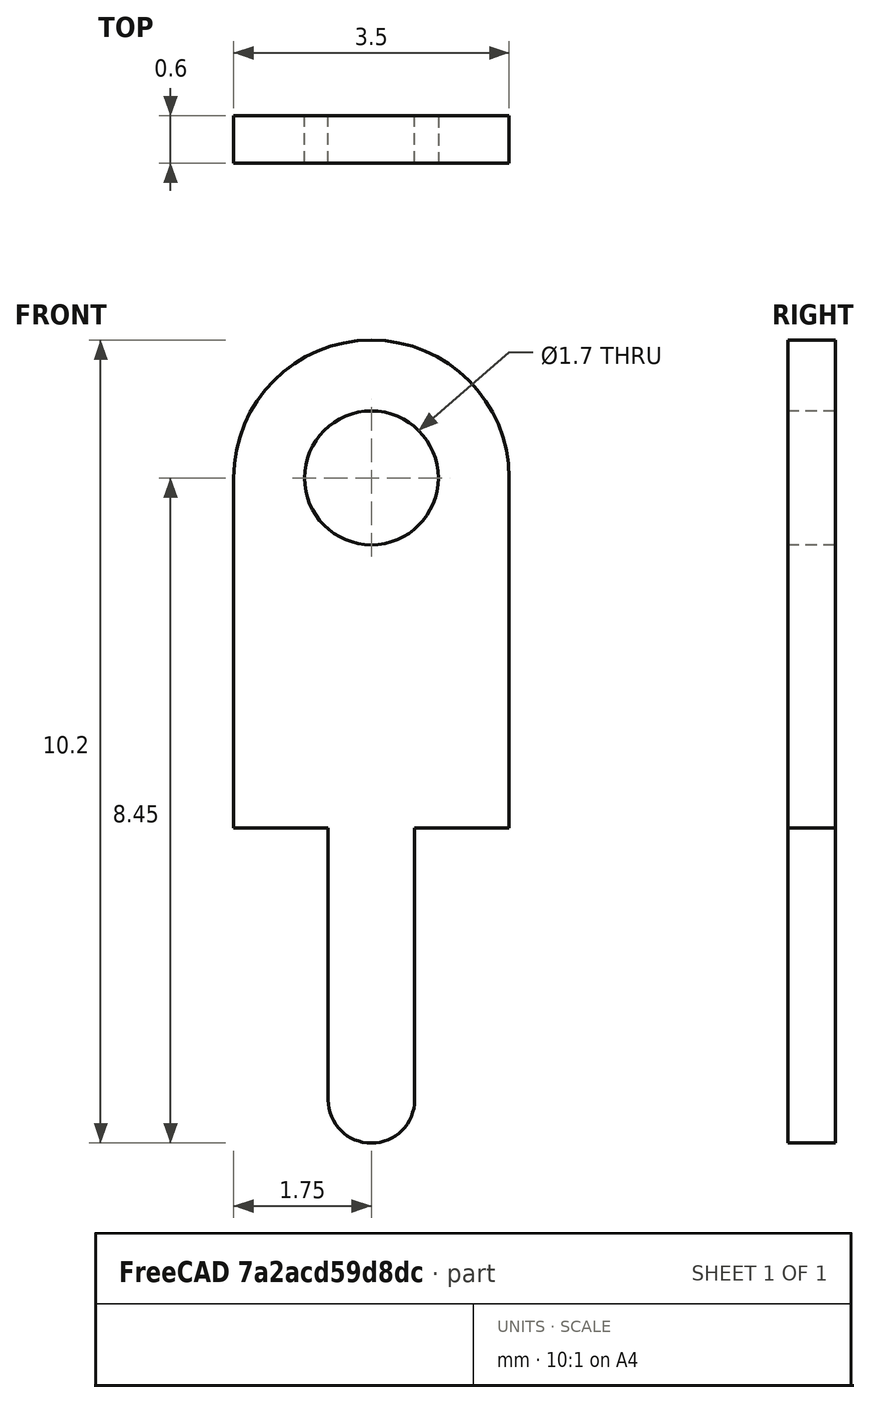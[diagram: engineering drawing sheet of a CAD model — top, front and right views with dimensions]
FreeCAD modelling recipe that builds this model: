
FCSTD DOCUMENT  (FreeCAD 0.17R12018 (Git))
Label: Pin_d1.1mm_L10.2mm_W3.5mm_Flat
License: All rights reserved
LicenseURL: http://en.wikipedia.org/wiki/All_rights_reserved
objects: Spreadsheet::Sheet×1, Sketcher::SketchObject×1, PartDesign::Pad×1, PartDesign::Body×1, App::Part×1
note: 4 computed .brp shape members not serialized (recipe doc carries the construction recipe); baked Part::Feature solids carry a one-line shape summary decoded from their .brp

FEATURE [Spreadsheet::Sheet] Spreadsheet  label="dimensions"
  cells = A1="L"; B1(L)=10.199999999999999; A2="Wtop"; B2(Wtop)=3.5; A3="Wbottom"; B3(Wbottom)=1.1000000000000001; A4="Lbottom"; B4(Lbottom)=4; A5="Wfork"; B5(Wfork)=1.7; A7="thick"; B7(thick)=0.59999999999999998
FEATURE [Sketcher::SketchObject] Sketch
  MapMode = 5
  Placement = pos=(0,0,0) rot=(0,0.707107,0.707107;3.14159rad)
  Support = -> [XZ_Plane001]
  expr: Constraints[19] = dimensions.Lbottom - dimensions.Wbottom / 2
  expr: Constraints[21] = (dimensions.Wtop - dimensions.Wbottom) / 2
  expr: Constraints[20] = dimensions.Wbottom
  expr: Constraints[14] = dimensions.L - dimensions.Lbottom - dimensions.Wtop / 2
  expr: Constraints[22] = dimensions.Wtop
  expr: Constraints[25] = dimensions.Wfork / 2
  sketch-geometry (11):
    g0: LineSegment StartX=-1.75 StartY=4.45 StartZ=0 EndX=-1.75 EndY=0 EndZ=0
    g1: LineSegment StartX=-1.75 StartY=0 StartZ=0 EndX=-0.55 EndY=0 EndZ=0
    g2: LineSegment StartX=-0.55 StartY=0 StartZ=0 EndX=-0.55 EndY=-3.45 EndZ=0
    g3: LineSegment StartX=0.55 StartY=0 StartZ=0 EndX=0.55 EndY=-3.45 EndZ=0
    g4: LineSegment StartX=0.55 StartY=0 StartZ=0 EndX=1.75 EndY=0 EndZ=0
    g5: LineSegment StartX=1.75 StartY=0 StartZ=0 EndX=1.75 EndY=4.45 EndZ=0
    g6: ArcOfCircle CenterX=0 CenterY=-3.45 CenterZ=0 NormalX=0 NormalY=0 NormalZ=1 Radius=0.55 StartAngle=3.14159 EndAngle=6.28319
    g7: LineSegment [constr] StartX=-0.55 StartY=-3.45 StartZ=0 EndX=0.55 EndY=-3.45 EndZ=0
    g8: Circle CenterX=0 CenterY=4.45 CenterZ=0 NormalX=0 NormalY=0 NormalZ=1 Radius=0.85
    g9: ArcOfCircle CenterX=0 CenterY=4.45 CenterZ=0 NormalX=0 NormalY=0 NormalZ=1 Radius=1.75 StartAngle=0 EndAngle=3.14159
    g10: LineSegment [constr] StartX=-1.75 StartY=4.45 StartZ=0 EndX=1.75 EndY=4.45 EndZ=0
  constraints (34):
    c: PointOnObject(g3,g-1)
    c: PointOnObject(g6,g-2)
    c: Coincident(g7,g3)
    c: Coincident(g7,g2)
    c: Coincident(g2,g6)
    c: Coincident(g3,g6)
    c: PointOnObject(g6,g7)
    c: Horizontal(g7)
    c: Vertical(g3)
    c: Vertical(g2)
    c: Horizontal(g1)
    c: Horizontal(g4)
    c: Vertical(g5)
    c: Vertical(g0)
    c: DistanceY(g5,g5) = 4.45
    c: Coincident(g5,g4)
    c: Coincident(g0,g1)
    c: Coincident(g4,g3)
    c: Coincident(g1,g2)
    c: DistanceY(g3,g3) = 3.45
    c: DistanceX(g2,g3) = 1.1
    c: DistanceX(g1,g1) = 1.2
    c: DistanceX(g0,g5) = 3.5
    c: PointOnObject(g1,g-1)
    c: PointOnObject(g8,g-2)
    c: Radius(g8) = 0.85
    c: PointOnObject(g9,g-2)
    c: Coincident(g9,g0)
    c: Coincident(g9,g5)
    c: Coincident(g10,g0)
    c: Coincident(g10,g5)
    c: Horizontal(g10)
    c: PointOnObject(g9,g10)
    c: PointOnObject(g8,g10)
FEATURE [PartDesign::Pad] Pad  label="Pin_d1.1mm_L10.2mm_W3.5mm_Flat"
  Length = 0.6
  Length2 = 100
  Midplane = true
  Placement = pos=(0,0,0) rot=(1,0,0;1.5708rad)
  Profile = -> Sketch
  Type = 0
  expr: Length = dimensions.thick
FEATURE [PartDesign::Body] PadBody  label="Body"
  Group = -> [Sketch,Pad]
  Origin = -> Origin001
  Tip = -> Pad
FEATURE [App::Part] Part
  Group = -> [PadBody]
  License = CC BY 3.0
  LicenseURL = http://creativecommons.org/licenses/by/3.0/
  Origin = -> Origin
